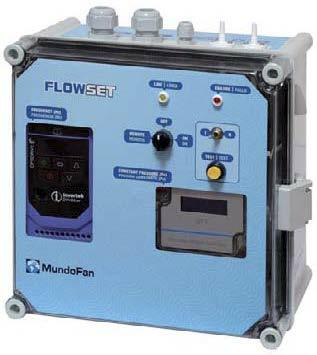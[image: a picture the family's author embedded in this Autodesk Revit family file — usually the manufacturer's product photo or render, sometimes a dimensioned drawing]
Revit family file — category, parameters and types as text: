
# Revit family: FLOWSET-15_VE10845
name_source: partatom
category: Aparatos eléctricos
revit_build: Autodesk Revit 2016 (Build: 20150220_1215(x64)
units: mm (PartAtom-declared; Revit-internal decimal feet)

## family parameters
Compartido = No
Corte con vacíos al cargar = No
Cota de conector redondo = Diámetro de uso
Mantener orientación de anotación = No
Número OmniClass = 23.80.00.00
Punto de cálculo de habitación = No
Se basa en plano de trabajo = No
Siempre vertical = Sí
Tipo de pieza = Caja de conexiones
Título OmniClass = Electric Power and Lighting

## types (1)
- FLOWSET
    Alimentación = 400Vac trifásico
    Corriente = 4,1 A
    Costo = 0 $
    Código de montaje = VE10845
    Descripción = CONTROL EFICIENCIA ENERGETICA PARA VENTILADORES - Caudal aire constante
    Dimensiones máx. = 270x300x170 mm
    Fabricante = SALVADOR ESCODA
    Imagen de tipo = flowset.jpg
    Leds = linea / fallo
    Modelo = FLOWSET 1,1kW
    Normativas = EN-ISO 14644-1:2000
    Potencia = 1,5 kW
    Regulación = Mediante sonda analógica de presión
    Salida = 400Vac trifásico
    Selector = 3 posiciones remoto / off / on
    URL = www.salvadorescoda.com
    Visualización = frecuencia (Hz) y presión (Pa)
